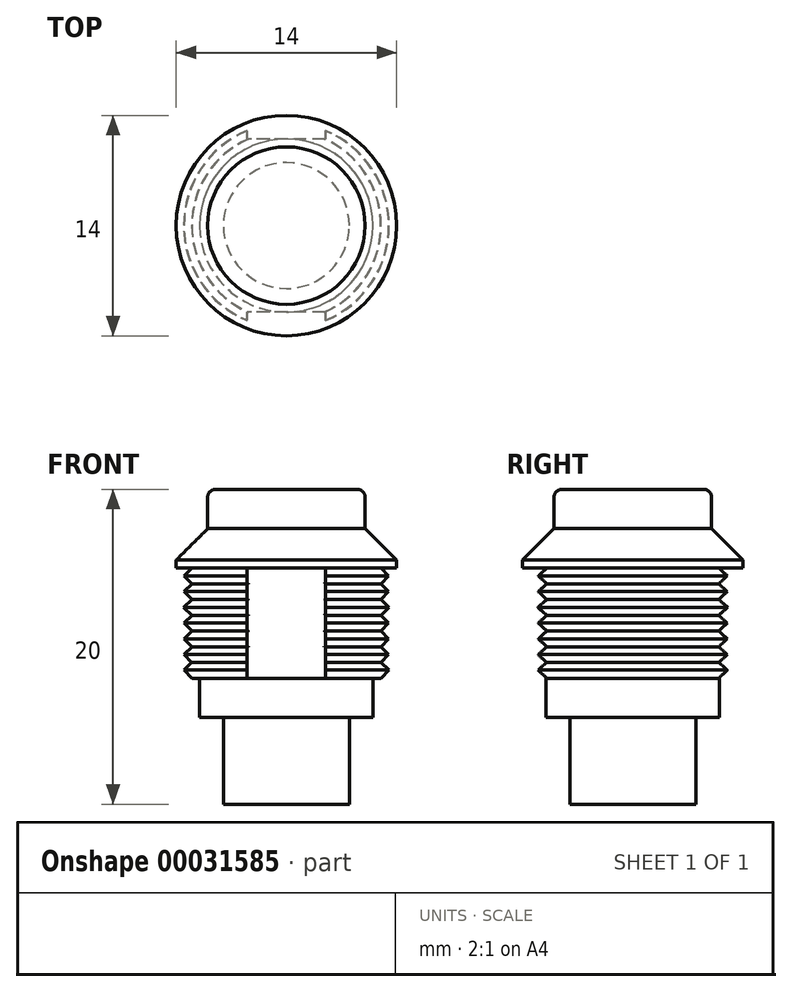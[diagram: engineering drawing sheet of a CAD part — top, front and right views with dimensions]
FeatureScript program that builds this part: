
annotation { "Feature Type Name" : "Feature", "Feature Type Description" : "" }
export const myFeature = defineFeature(function(context is Context, id is Id, definition is map)
    precondition{}
    {
        {
            var Q0;
            Q0=qCreatedBy(makeId("Front.planeOp"),FACE);
            var sketch = newSketch(context, id + "F0", { "sketchPlane" : qUnion([Q0])});
            skLineSegment(sketch, "E0", {"start": v(0, 0) * mm, "end": v(0, 17.79) * mm, "construction": true});
            skLineSegment(sketch, "E1", {"start": v(0, 0) * mm, "end": v(4, 0) * mm});
            skLineSegment(sketch, "E2", {"start": v(4, 0) * mm, "end": v(4, 5.5) * mm});
            skLineSegment(sketch, "E3", {"start": v(4, 5.5) * mm, "end": v(5.5, 5.5) * mm});
            skLineSegment(sketch, "E4", {"start": v(5.5, 5.5) * mm, "end": v(5.5, 8) * mm});
            skLineSegment(sketch, "E5", {"start": v(5.5, 8) * mm, "end": v(0, 8) * mm});
            skLineSegment(sketch, "E6", {"start": v(0, 8) * mm, "end": v(0, 0) * mm});
            skSolve(sketch);
        }
        {
            var Q0;
            Q0 = qSketchRegion(id + "F0", true);
            var Q1;
            Q1=sQuery(id+"F0.wireOp",EDGE,"E0");
            revolve(context, id + "F1", {"entities" : qUnion([Q0]), "axis" : qUnion([Q1]), "revolveType" : RevolveType.FULL});
        }
        {
            var Q0;
            Q0=qCreatedBy(makeId("Front.planeOp"),FACE);
            var sketch = newSketch(context, id + "F2", { "sketchPlane" : qUnion([Q0])});
            skLineSegment(sketch, "E7", {"start": v(0, 8) * mm, "end": v(0, 15) * mm});
            skLineSegment(sketch, "E8", {"start": v(0, 15) * mm, "end": v(6, 15) * mm});
            skLineSegment(sketch, "E9", {"start": v(6, 15) * mm, "end": v(6, 8) * mm});
            skLineSegment(sketch, "E10", {"start": v(6, 8) * mm, "end": v(0, 8) * mm});
            skLineSegment(sketch, "E11", {"start": v(0, 8) * mm, "end": v(0, 17.78) * mm, "construction": true});
            skSolve(sketch);
        }
        {
            var Q0;
            Q0=makeQuery(id+"F2.imprint","IMPRINT",FACE,{"disambiguationData":[TD([[makeQuery(id+"F2.imprint","IMPRINT",EDGE,{"derivedFrom":sQuery(id+"F2.wireOp",EDGE,"E7")}),-1.0]])]});
            var Q1;
            Q1=sQuery(id+"F2.wireOp",EDGE,"E11");
            revolve(context, id + "F3", {"operationType" : NewBodyOperationType.ADD, "entities" : qUnion([Q0]), "axis" : qUnion([Q1]), "revolveType" : RevolveType.FULL});
        }
        {
            var Q0;
            Q0=qCreatedBy(makeId("Top.planeOp"),FACE);
            cPlane(context, id + "F4", {"entities" : qUnion([Q0]), "cplaneType" : CPlaneType.OFFSET, "offset" : 6 * mm, "width" : 150 * mm, "height" : 150 * mm});
        }
        {
            var Q0;
            Q0=qCreatedBy(id+"F4.planeOp",FACE);
            var sketch = newSketch(context, id + "F5", { "sketchPlane" : qUnion([Q0])});
            skCircle(sketch, "E12", {"center": v(0, 0) * mm, "radius": 6.25 * mm});
            skSolve(sketch);
        }
        {
            var Q0;
            Q0=qCreatedBy(makeId("Front.planeOp"),FACE);
            var sketch = newSketch(context, id + "F6", { "sketchPlane" : qUnion([Q0])});
            skLineSegment(sketch, "E13.0", {"start": v(-0.01, 8.51) * mm, "end": v(-6.51, 8.51) * mm, "construction": true});
            skLineSegment(sketch, "E14", {"start": v(-6, 8) * mm, "end": v(-6.51, 8.51) * mm});
            skLineSegment(sketch, "E15", {"start": v(-6.02, 9) * mm, "end": v(-6.51, 8.51) * mm});
            skLineSegment(sketch, "E16", {"start": v(0, 8) * mm, "end": v(0, 11.23) * mm, "construction": true});
            skLineSegment(sketch, "E17", {"start": v(-6, 8) * mm, "end": v(0, 8) * mm});
            skLineSegment(sketch, "E18", {"start": v(-6, 10) * mm, "end": v(-6.5, 9.5) * mm});
            skLineSegment(sketch, "E19", {"start": v(-6.02, 9) * mm, "end": v(-6.5, 9.5) * mm});
            skLineSegment(sketch, "E20", {"start": v(-6, 10) * mm, "end": v(-6.5, 10.5) * mm});
            skLineSegment(sketch, "E21", {"start": v(-6.5, 10.5) * mm, "end": v(-6, 11) * mm});
            skLineSegment(sketch, "E22", {"start": v(-6, 11) * mm, "end": v(-6.5, 11.5) * mm});
            skLineSegment(sketch, "E23", {"start": v(-6.5, 11.5) * mm, "end": v(-6, 12) * mm});
            skLineSegment(sketch, "E24", {"start": v(-6, 12) * mm, "end": v(-6.53, 12.5) * mm});
            skLineSegment(sketch, "E25", {"start": v(-6.53, 12.5) * mm, "end": v(-6, 13) * mm});
            skLineSegment(sketch, "E26", {"start": v(-6, 13) * mm, "end": v(-6.5, 13.5) * mm});
            skLineSegment(sketch, "E27", {"start": v(-6.5, 13.5) * mm, "end": v(-6, 14) * mm});
            skLineSegment(sketch, "E28", {"start": v(-6, 14) * mm, "end": v(-6.5, 14.5) * mm});
            skLineSegment(sketch, "E29", {"start": v(-6.5, 14.5) * mm, "end": v(-6, 15) * mm});
            skLineSegment(sketch, "E30", {"start": v(-6, 15) * mm, "end": v(0, 15) * mm});
            skLineSegment(sketch, "E31", {"start": v(0, 15) * mm, "end": v(0, 8) * mm});
            skSolve(sketch);
        }
        {
            var Q0;
            Q0=makeQuery(id+"F6.imprint","IMPRINT",FACE,{"disambiguationData":[TD([[makeQuery(id+"F6.imprint","IMPRINT",EDGE,{"derivedFrom":sQuery(id+"F6.wireOp",EDGE,"E14")}),-1.0]])]});
            var Q1;
            Q1=sQuery(id+"F6.wireOp",EDGE,"E16");
            revolve(context, id + "F7", {"operationType" : NewBodyOperationType.ADD, "entities" : qUnion([Q0]), "axis" : qUnion([Q1]), "revolveType" : RevolveType.FULL});
        }
        {
            var Q0;
            Q0=qCreatedBy(makeId("Front.planeOp"),FACE);
            var sketch = newSketch(context, id + "F8", { "sketchPlane" : qUnion([Q0])});
            skLineSegment(sketch, "E32", {"start": v(0, 15) * mm, "end": v(0, 20) * mm});
            skLineSegment(sketch, "E33", {"start": v(0, 15) * mm, "end": v(-7, 15) * mm});
            skLineSegment(sketch, "E34", {"start": v(-7, 15) * mm, "end": v(-7, 17.5) * mm});
            skLineSegment(sketch, "E35", {"start": v(-7, 17.5) * mm, "end": v(-5, 17.5) * mm});
            skLineSegment(sketch, "E36", {"start": v(-5, 17.5) * mm, "end": v(-5, 20) * mm});
            skLineSegment(sketch, "E37", {"start": v(-5, 20) * mm, "end": v(0, 20) * mm});
            skLineSegment(sketch, "E38", {"start": v(0, 15) * mm, "end": v(0, 22.94) * mm, "construction": true});
            skSolve(sketch);
        }
        {
            var Q0;
            Q0=makeQuery(id+"F8.imprint","IMPRINT",FACE,{"disambiguationData":[TD([[makeQuery(id+"F8.imprint","IMPRINT",EDGE,{"derivedFrom":sQuery(id+"F8.wireOp",EDGE,"E32")}),1.0]])]});
            var Q1;
            Q1=sQuery(id+"F8.wireOp",EDGE,"E38");
            var Q2;
            Q2=sQuery(id+"F8.wireOp",EDGE,"E38");
            revolve(context, id + "F9", {"operationType" : NewBodyOperationType.ADD, "entities" : qUnion([Q0]), "surfaceEntities" : qUnion([Q1]), "axis" : qUnion([Q2]), "revolveType" : RevolveType.FULL});
        }
        {
            var Q0;
            Q0=makeQuery(id+"F9.opRevolve","SWEPT_EDGE",EDGE,{"disambiguationData":[OSD([sQuery(id+"F8.wireOp",EDGE,"E34"),sQuery(id+"F8.wireOp",EDGE,"E35")])]});
            chamfer(context, id + "F10", {"entities" : qUnion([Q0]), "chamferType" : ChamferType.TWO_OFFSETS, "width1" : 2 * mm, "oppositeDirection" : false, "width2" : 2 * mm, "tangentPropagation" : true});
        }
        {
            var Q0;
            Q0=makeQuery(id+"F9.opRevolve","SWEPT_EDGE",EDGE,{"disambiguationData":[OSD([sQuery(id+"F8.wireOp",EDGE,"E36"),sQuery(id+"F8.wireOp",EDGE,"E37")])]});
            fillet(context, id + "F11", {"entities" : qUnion([Q0]), "radius" : 0.5 * mm, "tangentPropagation" : true, "allowEdgeOverflow" : false});
        }
        {
            var Q0;
            Q0=qCreatedBy(makeId("Top.planeOp"),FACE);
            var sketch = newSketch(context, id + "F12", { "sketchPlane" : qUnion([Q0])});
            skLineSegment(sketch, "E39.bottom", {"start": v(-2.5, 8.9) * mm, "end": v(2.5, 8.9) * mm});
            skLineSegment(sketch, "E39.top", {"start": v(-2.5, 5.5) * mm, "end": v(2.5, 5.5) * mm});
            skLineSegment(sketch, "E39.left", {"start": v(-2.5, 8.9) * mm, "end": v(-2.5, 5.5) * mm});
            skLineSegment(sketch, "E39.right", {"start": v(2.5, 8.9) * mm, "end": v(2.5, 5.5) * mm});
            skLineSegment(sketch, "E40.bottom", {"start": v(-2.5, -5.5) * mm, "end": v(2.5, -5.5) * mm});
            skLineSegment(sketch, "E40.top", {"start": v(-2.5, -9.78) * mm, "end": v(2.5, -9.78) * mm});
            skLineSegment(sketch, "E40.left", {"start": v(-2.5, -5.5) * mm, "end": v(-2.5, -9.78) * mm});
            skLineSegment(sketch, "E40.right", {"start": v(2.5, -5.5) * mm, "end": v(2.5, -9.78) * mm});
            skSolve(sketch);
        }
        {
            var Q0;
            Q0 = qSketchRegion(id + "F12", true);
            var Q1;
            Q1=makeQuery(id+"F9.opRevolve","SWEPT_FACE",FACE,{"disambiguationData":[OSD([sQuery(id+"F8.wireOp",EDGE,"E33")])]});
            extrude(context, id + "F13", {"entities" : qUnion([Q0]), "operationType" : NewBodyOperationType.REMOVE, "endBound" : BoundingType.UP_TO_SURFACE, "endBoundEntityFace" : qUnion([Q1]), "depth" : 25 * mm});
        }
    });
